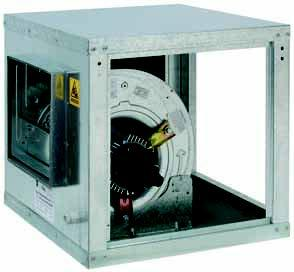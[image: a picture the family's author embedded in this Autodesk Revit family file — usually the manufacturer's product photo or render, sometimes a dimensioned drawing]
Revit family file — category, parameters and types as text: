
# Revit family: BD-ERP_25-25-M4
name_source: partatom
category: Aparatos eléctricos
revit_build: Autodesk Revit 2016 (Build: 20150220_1215(x64)
units: mm (PartAtom-declared; Revit-internal decimal feet)

## family parameters
Compartido = No
Corte con vacíos al cargar = No
Cota de conector redondo = Diámetro de uso
Mantener orientación de anotación = No
Número OmniClass = 23.80.00.00
Punto de cálculo de habitación = No
Se basa en plano de trabajo = No
Siempre vertical = Sí
Tipo de pieza = Caja de conexiones
Título OmniClass = Electric Power and Lighting

## types (1)
- BD ERP
    Caudal máx. = 1900 m3/h
    Clase = F
    Costo = 0 $
    Código de montaje = CV01624
    Descripción = CAJAS DE VENTILACIÓN CON MOTOR INCORPORADO
    Dimensiones exteriores = 500 x 490 x 490 mm
    Dimensiones ventana = Ø350 mm
    Fabricante = SALVADOR ESCODA
    Imagen de tipo = CajasVentilacion-BD-ERP.jpg
    Intensidad abs. monof. 50Hz-230V = 0,77 A
    Modelo = BD ERP 25/25 M4 CIRCULAR
    Nivel presión sonora = 54 db(A)
    Peso = 20 Kg
    Potencia motor = 0,12 kW
    Protección = IP-55
    URL = www.salvadorescoda.com
    Velocidad = 925 rpm
